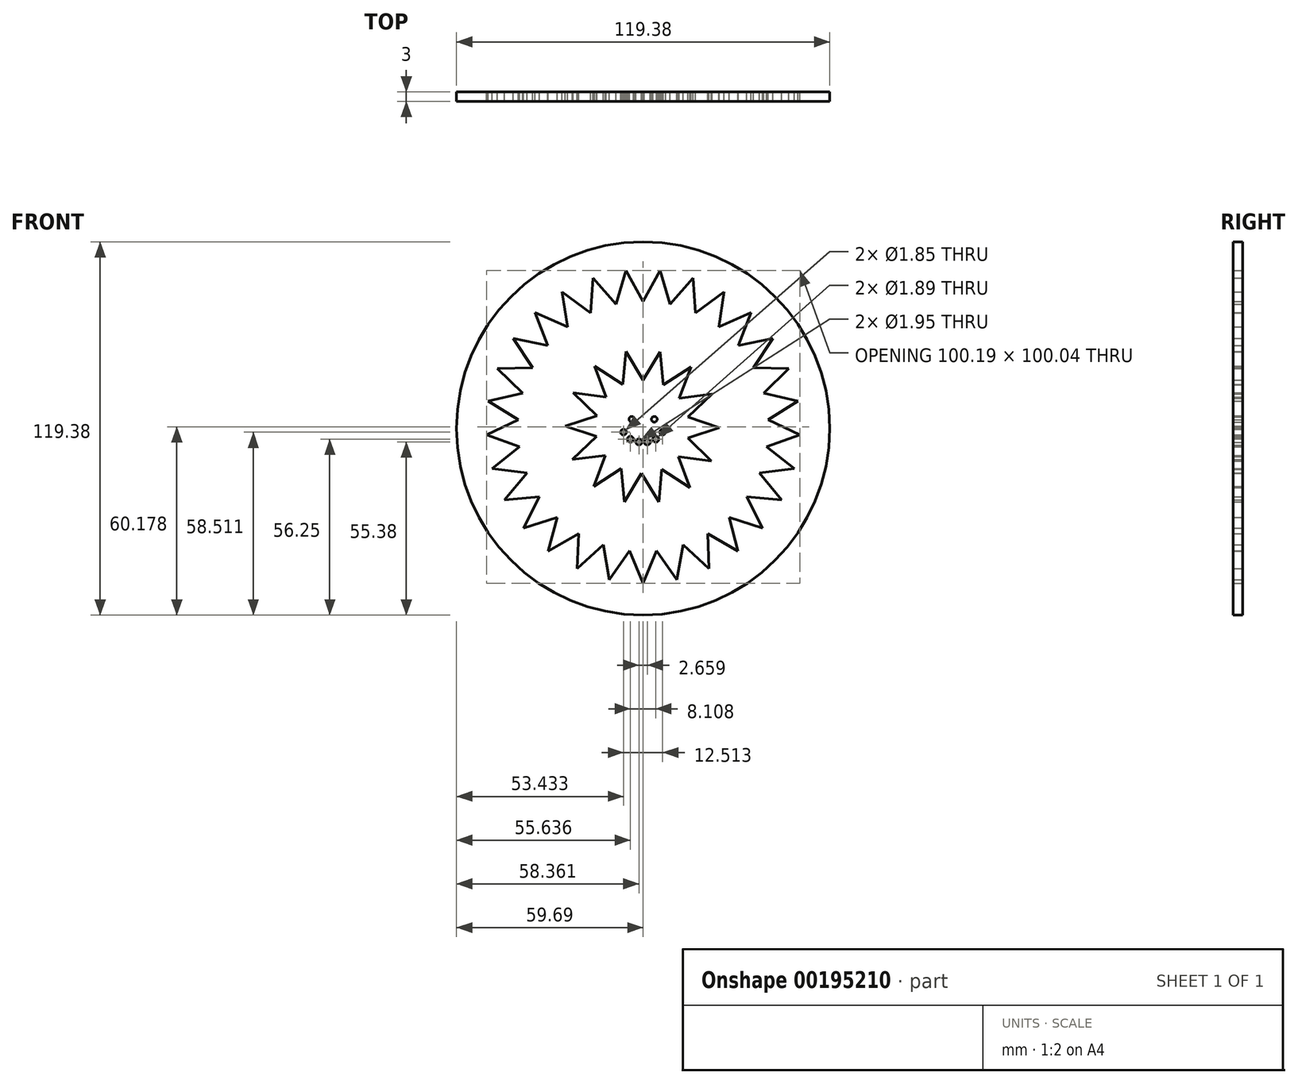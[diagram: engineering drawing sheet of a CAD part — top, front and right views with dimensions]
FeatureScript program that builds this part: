
annotation { "Feature Type Name" : "Feature", "Feature Type Description" : "" }
export const myFeature = defineFeature(function(context is Context, id is Id, definition is map)
    precondition{}
    {
        {
            var Q0;
            Q0=qCreatedBy(makeId("Front.planeOp"),FACE);
            var sketch = newSketch(context, id + "F0", { "sketchPlane" : qUnion([Q0])});
            skLineSegment(sketch, "E0", {"start": v(0, 40.64) * mm, "end": v(5.42, 50.5) * mm});
            skLineSegment(sketch, "E1", {"start": v(0, 40.64) * mm, "end": v(-5.42, 50.5) * mm});
            skLineSegment(sketch, "E2.1.0", {"start": v(-8.6, 39.7) * mm, "end": v(-5.42, 50.5) * mm});
            skLineSegment(sketch, "E2.1.1", {"start": v(-8.6, 39.7) * mm, "end": v(-16.02, 48.18) * mm});
            skLineSegment(sketch, "E2.2.0", {"start": v(-16.8, 36.94) * mm, "end": v(-16.02, 48.18) * mm});
            skLineSegment(sketch, "E2.2.1", {"start": v(-16.8, 36.94) * mm, "end": v(-25.86, 43.62) * mm});
            skLineSegment(sketch, "E2.3.0", {"start": v(-24.21, 32.48) * mm, "end": v(-25.86, 43.62) * mm});
            skLineSegment(sketch, "E2.3.1", {"start": v(-24.21, 32.48) * mm, "end": v(-34.5, 37.06) * mm});
            skLineSegment(sketch, "E2.4.0", {"start": v(-30.5, 26.53) * mm, "end": v(-34.5, 37.06) * mm});
            skLineSegment(sketch, "E2.4.1", {"start": v(-30.5, 26.53) * mm, "end": v(-41.52, 28.79) * mm});
            skLineSegment(sketch, "E2.5.0", {"start": v(-35.35, 19.37) * mm, "end": v(-41.52, 28.79) * mm});
            skLineSegment(sketch, "E2.5.1", {"start": v(-35.35, 19.37) * mm, "end": v(-46.6, 19.2) * mm});
            skLineSegment(sketch, "E2.6.0", {"start": v(-38.55, 11.34) * mm, "end": v(-46.6, 19.2) * mm});
            skLineSegment(sketch, "E2.6.1", {"start": v(-38.55, 11.34) * mm, "end": v(-49.5, 8.75) * mm});
            skLineSegment(sketch, "E2.7.0", {"start": v(-39.95, 2.8) * mm, "end": v(-49.5, 8.75) * mm});
            skLineSegment(sketch, "E2.7.1", {"start": v(-39.95, 2.8) * mm, "end": v(-50.1, -2.08) * mm});
            skLineSegment(sketch, "E2.8.0", {"start": v(-39.48, -5.84) * mm, "end": v(-50.1, -2.08) * mm});
            skLineSegment(sketch, "E2.8.1", {"start": v(-39.48, -5.84) * mm, "end": v(-48.34, -12.79) * mm});
            skLineSegment(sketch, "E2.9.0", {"start": v(-37.16, -14.17) * mm, "end": v(-48.34, -12.79) * mm});
            skLineSegment(sketch, "E2.9.1", {"start": v(-37.16, -14.17) * mm, "end": v(-44.32, -22.86) * mm});
            skLineSegment(sketch, "E2.10.0", {"start": v(-33.11, -21.82) * mm, "end": v(-44.32, -22.86) * mm});
            skLineSegment(sketch, "E2.10.1", {"start": v(-33.11, -21.82) * mm, "end": v(-38.24, -31.84) * mm});
            skLineSegment(sketch, "E2.11.0", {"start": v(-27.51, -28.4) * mm, "end": v(-38.24, -31.84) * mm});
            skLineSegment(sketch, "E2.11.1", {"start": v(-27.51, -28.4) * mm, "end": v(-30.36, -39.3) * mm});
            skLineSegment(sketch, "E2.12.0", {"start": v(-20.62, -33.64) * mm, "end": v(-30.36, -39.3) * mm});
            skLineSegment(sketch, "E2.12.1", {"start": v(-20.62, -33.64) * mm, "end": v(-21.07, -44.9) * mm});
            skLineSegment(sketch, "E2.13.0", {"start": v(-12.77, -37.28) * mm, "end": v(-21.07, -44.9) * mm});
            skLineSegment(sketch, "E2.13.1", {"start": v(-12.77, -37.28) * mm, "end": v(-10.78, -48.36) * mm});
            skLineSegment(sketch, "E2.14.0", {"start": v(-4.33, -39.14) * mm, "end": v(-10.78, -48.36) * mm});
            skLineSegment(sketch, "E2.14.1", {"start": v(-4.33, -39.14) * mm, "end": v(0, -49.53) * mm});
            skLineSegment(sketch, "E2.15.0", {"start": v(4.33, -39.14) * mm, "end": v(0, -49.53) * mm});
            skLineSegment(sketch, "E2.15.1", {"start": v(4.33, -39.14) * mm, "end": v(10.78, -48.36) * mm});
            skLineSegment(sketch, "E2.16.0", {"start": v(12.77, -37.28) * mm, "end": v(10.78, -48.36) * mm});
            skLineSegment(sketch, "E2.16.1", {"start": v(12.77, -37.28) * mm, "end": v(21.07, -44.9) * mm});
            skLineSegment(sketch, "E2.17.0", {"start": v(20.62, -33.64) * mm, "end": v(21.07, -44.9) * mm});
            skLineSegment(sketch, "E2.17.1", {"start": v(20.62, -33.64) * mm, "end": v(30.36, -39.3) * mm});
            skLineSegment(sketch, "E2.18.0", {"start": v(27.51, -28.4) * mm, "end": v(30.36, -39.3) * mm});
            skLineSegment(sketch, "E2.18.1", {"start": v(27.51, -28.4) * mm, "end": v(38.24, -31.84) * mm});
            skLineSegment(sketch, "E2.19.0", {"start": v(33.11, -21.82) * mm, "end": v(38.24, -31.84) * mm});
            skLineSegment(sketch, "E2.19.1", {"start": v(33.11, -21.82) * mm, "end": v(44.32, -22.86) * mm});
            skLineSegment(sketch, "E2.20.0", {"start": v(37.16, -14.17) * mm, "end": v(44.32, -22.86) * mm});
            skLineSegment(sketch, "E2.20.1", {"start": v(37.16, -14.17) * mm, "end": v(48.34, -12.79) * mm});
            skLineSegment(sketch, "E2.21.0", {"start": v(39.48, -5.84) * mm, "end": v(48.34, -12.79) * mm});
            skLineSegment(sketch, "E2.21.1", {"start": v(39.48, -5.84) * mm, "end": v(50.1, -2.08) * mm});
            skLineSegment(sketch, "E2.22.0", {"start": v(39.95, 2.8) * mm, "end": v(50.1, -2.08) * mm});
            skLineSegment(sketch, "E2.22.1", {"start": v(39.95, 2.8) * mm, "end": v(49.5, 8.75) * mm});
            skLineSegment(sketch, "E2.23.0", {"start": v(38.55, 11.34) * mm, "end": v(49.5, 8.75) * mm});
            skLineSegment(sketch, "E2.23.1", {"start": v(38.55, 11.34) * mm, "end": v(46.6, 19.2) * mm});
            skLineSegment(sketch, "E2.24.0", {"start": v(35.35, 19.37) * mm, "end": v(46.6, 19.2) * mm});
            skLineSegment(sketch, "E2.24.1", {"start": v(35.35, 19.37) * mm, "end": v(41.52, 28.79) * mm});
            skLineSegment(sketch, "E2.25.0", {"start": v(30.5, 26.53) * mm, "end": v(41.52, 28.79) * mm});
            skLineSegment(sketch, "E2.25.1", {"start": v(30.5, 26.53) * mm, "end": v(34.5, 37.06) * mm});
            skLineSegment(sketch, "E2.26.0", {"start": v(24.21, 32.48) * mm, "end": v(34.5, 37.06) * mm});
            skLineSegment(sketch, "E2.26.1", {"start": v(24.21, 32.48) * mm, "end": v(25.86, 43.62) * mm});
            skLineSegment(sketch, "E2.27.0", {"start": v(16.8, 36.94) * mm, "end": v(25.86, 43.62) * mm});
            skLineSegment(sketch, "E2.27.1", {"start": v(16.8, 36.94) * mm, "end": v(16.02, 48.18) * mm});
            skLineSegment(sketch, "E2.28.0", {"start": v(8.6, 39.7) * mm, "end": v(16.02, 48.18) * mm});
            skLineSegment(sketch, "E2.28.1", {"start": v(8.6, 39.7) * mm, "end": v(5.42, 50.5) * mm});
            skCircle(sketch, "E3", {"center": v(0, 0) * mm, "radius": 59.7 * mm});
            skCircle(sketch, "E4", {"center": v(-3.6, 2.94) * mm, "radius": 0.91 * mm});
            skCircle(sketch, "E5.MirrorC", {"center": v(3.6, 2.94) * mm, "radius": 0.91 * mm});
            skCircle(sketch, "E6", {"center": v(-6.26, -1.18) * mm, "radius": 0.92 * mm});
            skCircle(sketch, "E7", {"center": v(-4.05, -3.44) * mm, "radius": 0.95 * mm});
            skCircle(sketch, "E8", {"center": v(-1.33, -4.3) * mm, "radius": 0.97 * mm});
            skCircle(sketch, "E9.MirrorC", {"center": v(6.26, -1.18) * mm, "radius": 0.92 * mm});
            skCircle(sketch, "E10.MirrorC", {"center": v(4.05, -3.44) * mm, "radius": 0.95 * mm});
            skCircle(sketch, "E11.MirrorC", {"center": v(1.33, -4.3) * mm, "radius": 0.97 * mm});
            skLineSegment(sketch, "E12", {"start": v(0, 25.4) * mm, "end": v(0, 15.5) * mm});
            skLineSegment(sketch, "E13", {"start": v(0, 15.5) * mm, "end": v(5.6, 24.77) * mm});
            skLineSegment(sketch, "E14.MirrorCS", {"start": v(0, 15.5) * mm, "end": v(-5.6, 24.77) * mm});
            skLineSegment(sketch, "E15.1.0", {"start": v(-6.51, 14.12) * mm, "end": v(-5.5, 24.91) * mm});
            skLineSegment(sketch, "E15.1.1", {"start": v(-6.51, 14.12) * mm, "end": v(-15.59, 20.05) * mm});
            skLineSegment(sketch, "E15.2.0", {"start": v(-11.79, 10.06) * mm, "end": v(-15.55, 20.23) * mm});
            skLineSegment(sketch, "E15.2.1", {"start": v(-11.79, 10.06) * mm, "end": v(-22.54, 11.47) * mm});
            skLineSegment(sketch, "E15.3.0", {"start": v(-14.77, 4.11) * mm, "end": v(-22.58, 11.64) * mm});
            skLineSegment(sketch, "E15.3.1", {"start": v(-14.77, 4.11) * mm, "end": v(-25.07, 0.72) * mm});
            skLineSegment(sketch, "E15.4.0", {"start": v(-14.89, -2.54) * mm, "end": v(-25.18, 0.86) * mm});
            skLineSegment(sketch, "E15.4.1", {"start": v(-14.89, -2.54) * mm, "end": v(-22.69, -10.07) * mm});
            skLineSegment(sketch, "E15.5.0", {"start": v(-12.1, -8.59) * mm, "end": v(-22.85, -10) * mm});
            skLineSegment(sketch, "E15.5.1", {"start": v(-12.1, -8.59) * mm, "end": v(-15.86, -18.75) * mm});
            skLineSegment(sketch, "E15.6.0", {"start": v(-6.97, -12.82) * mm, "end": v(-16.04, -18.75) * mm});
            skLineSegment(sketch, "E15.6.1", {"start": v(-6.97, -12.82) * mm, "end": v(-5.95, -23.62) * mm});
            skLineSegment(sketch, "E15.7.0", {"start": v(-0.5, -14.41) * mm, "end": v(-6.1, -23.7) * mm});
            skLineSegment(sketch, "E15.7.1", {"start": v(-0.5, -14.41) * mm, "end": v(5.1, -23.7) * mm});
            skLineSegment(sketch, "E15.8.0", {"start": v(6, -13.04) * mm, "end": v(4.99, -23.83) * mm});
            skLineSegment(sketch, "E15.8.1", {"start": v(6, -13.04) * mm, "end": v(15.08, -18.97) * mm});
            skLineSegment(sketch, "E15.9.0", {"start": v(11.28, -8.98) * mm, "end": v(15.05, -19.15) * mm});
            skLineSegment(sketch, "E15.9.1", {"start": v(11.28, -8.98) * mm, "end": v(22.03, -10.39) * mm});
            skLineSegment(sketch, "E15.10.0", {"start": v(14.27, -3.03) * mm, "end": v(22.07, -10.56) * mm});
            skLineSegment(sketch, "E15.10.1", {"start": v(14.27, -3.03) * mm, "end": v(24.57, 0.36) * mm});
            skLineSegment(sketch, "E15.11.0", {"start": v(14.38, 3.62) * mm, "end": v(24.68, 0.23) * mm});
            skLineSegment(sketch, "E15.11.1", {"start": v(14.38, 3.62) * mm, "end": v(22.18, 11.15) * mm});
            skLineSegment(sketch, "E15.12.0", {"start": v(11.6, 9.67) * mm, "end": v(22.35, 11.07) * mm});
            skLineSegment(sketch, "E15.12.1", {"start": v(11.6, 9.67) * mm, "end": v(15.36, 19.83) * mm});
            skLineSegment(sketch, "E15.13.0", {"start": v(6.46, 13.9) * mm, "end": v(15.54, 19.83) * mm});
            skLineSegment(sketch, "E15.13.1", {"start": v(6.46, 13.9) * mm, "end": v(5.44, 24.7) * mm});
            skPoint(sketch, "E15.center", {"position": v(-0.25, 0.54) * mm});
            skSolve(sketch);
        }
        {
            var Q0;
            Q0=makeQuery(id+"F0.imprint","IMPRINT",FACE,{"disambiguationData":[TD([[makeQuery(id+"F0.imprint","IMPRINT",EDGE,{"derivedFrom":sQuery(id+"F0.wireOp",EDGE,"E0")}),1.0]])]});
            var Q1;
            Q1=makeQuery(id+"F0.imprint","IMPRINT",FACE,{"disambiguationData":[TD([[makeQuery(id+"F0.imprint","IMPRINT",EDGE,{"derivedFrom":sQuery(id+"F0.wireOp",EDGE,"E4")}),-1.0]])]});
            extrude(context, id + "F1", {"entities" : qUnion([Q0, Q1]), "depth" : 3 * mm});
        }
    });
